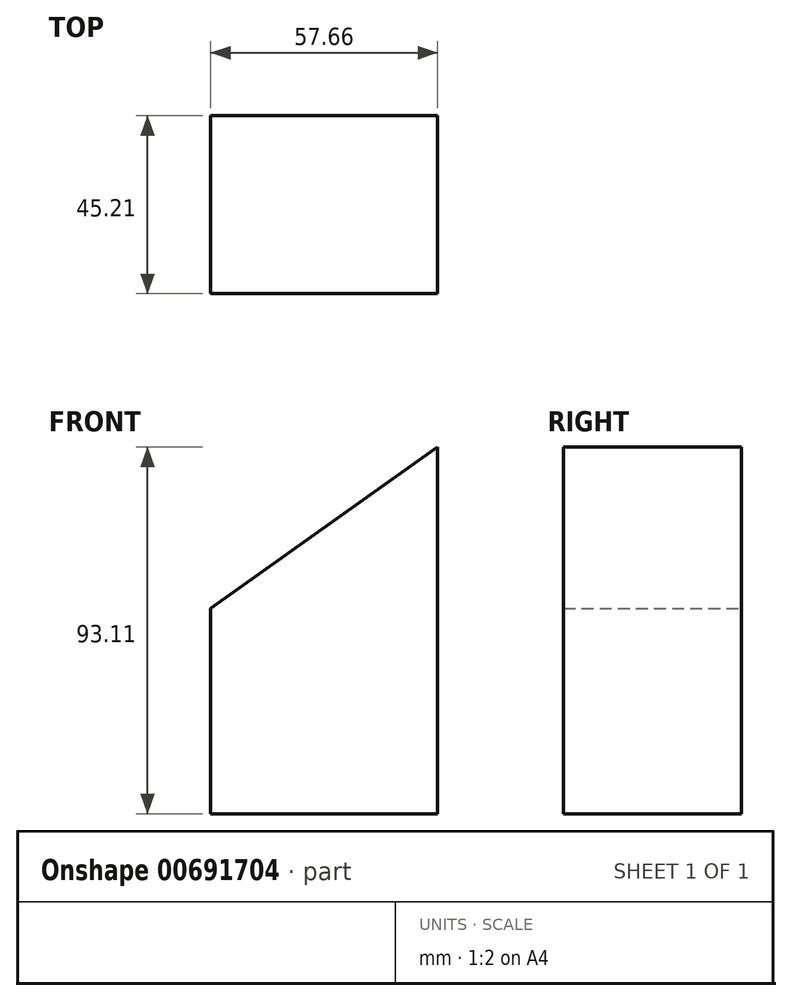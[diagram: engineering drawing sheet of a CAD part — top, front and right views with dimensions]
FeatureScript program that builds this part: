
annotation { "Feature Type Name" : "Feature", "Feature Type Description" : "" }
export const myFeature = defineFeature(function(context is Context, id is Id, definition is map)
    precondition{}
    {
        {
            var Q0;
            Q0=qCreatedBy(makeId("Front.planeOp"),FACE);
            var sketch = newSketch(context, id + "F0", { "sketchPlane" : qUnion([Q0])});
            skLineSegment(sketch, "E0", {"start": v(-54.11, 33.38) * mm, "end": v(-54.11, -18.73) * mm});
            skLineSegment(sketch, "E1", {"start": v(-54.11, 33.38) * mm, "end": v(3.55, 33.38) * mm});
            skLineSegment(sketch, "E2", {"start": v(3.55, 33.38) * mm, "end": v(3.55, -18.73) * mm});
            skLineSegment(sketch, "E3", {"start": v(-54.11, -18.73) * mm, "end": v(3.55, -18.73) * mm});
            skLineSegment(sketch, "E4", {"start": v(3.55, 33.38) * mm, "end": v(3.55, 74.38) * mm});
            skLineSegment(sketch, "E5", {"start": v(-54.11, 33.38) * mm, "end": v(3.55, 74.38) * mm});
            skSolve(sketch);
        }
        {
            var Q0;
            Q0 = qSketchRegion(id + "F0", true);
            extrude(context, id + "F1", {"entities" : qUnion([Q0]), "depth" : 45.2 * mm, "offsetDistance" : 25.4 * mm});
        }
    });
